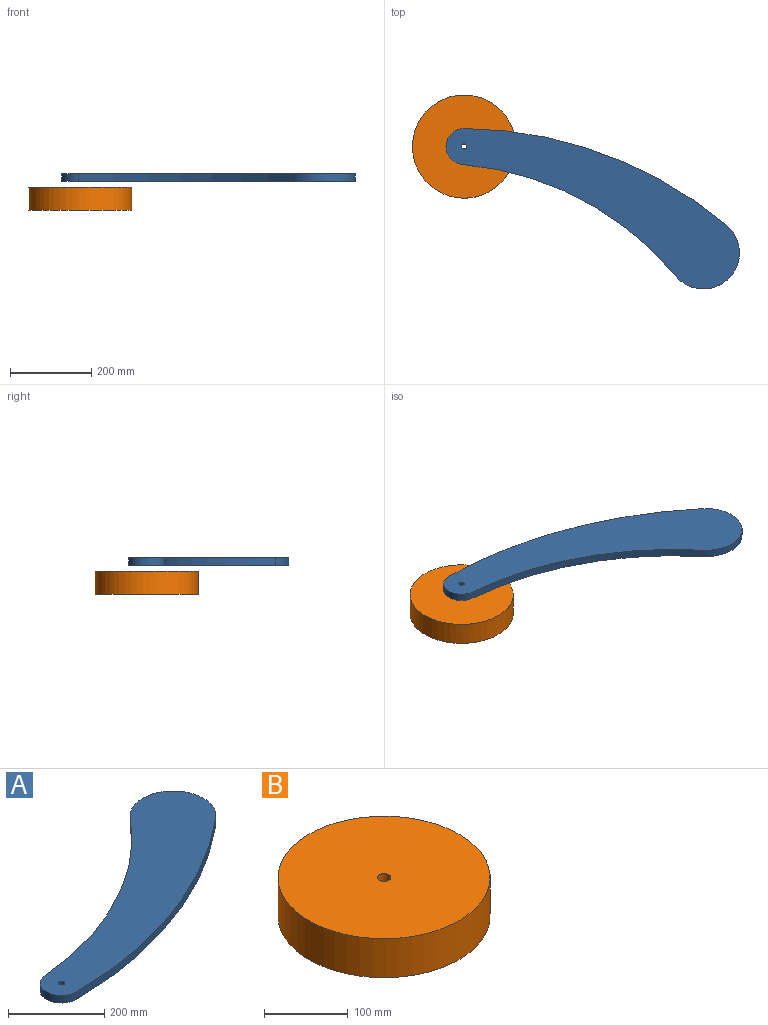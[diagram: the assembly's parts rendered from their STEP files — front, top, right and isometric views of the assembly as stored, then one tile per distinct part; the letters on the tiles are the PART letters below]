
ASSEMBLY  parts=2 mates=1
PART A: 7 faces, bbox 722.5x395.1x19.1 mm
  f0: cylinder r=44.45mm len=88.75mm, axis (0,0,-1), area 2596.3mm2, adj f1,f4,f5,f6
  f1: cylinder r=1016mm len=646.01mm, axis (0,0,-1), area 13380.8mm2, adj f0,f2,f5,f6
  f2: cylinder r=88.9mm len=157.44mm, axis (0,0,-1), area 5627.8mm2, adj f1,f4,f5,f6
  f3: cylinder r=6.35mm len=19.05mm, axis (0,0,-1), area 760.1mm2, adj f5,f6
  f4: cylinder r=762mm len=524.3mm, axis (0,0,-1), area 11574.3mm2, adj f0,f2,f5,f6
  f5: plane 722.5x395.09mm, normal (0,0,1), area 99722.6mm2, adj f0,f1,f2,f3,f4
  f6: plane 722.5x395.09mm, normal (0,0,-1), area 99722.6mm2, adj f0,f1,f2,f3,f4
PART B: 4 faces, bbox 254x254x57.2 mm
  f0: cylinder r=127mm len=254mm, axis (0,0,-1), area 45603.7mm2, adj f1,f2
  f1: plane 254x254mm, normal (0,0,1), area 50472.8mm2, adj f0,f3
  f2: plane 254x254mm, normal (0,0,-1), area 50472.8mm2, adj f0,f3
  f3: cylinder r=7.94mm len=57.15mm, axis (0,0,1), area 2850.2mm2, adj f1,f2
PLACE A rot(axis=(1,0,0),180deg) t=(-97.79,-41.42,84.14)mm
PLACE B t=(-97.79,-41.42,-6.02)mm fixed
MATE slider A.f0 <-> B.f3  axis (0,0,-1) through (-97.79,-41.42,65.09)mm
